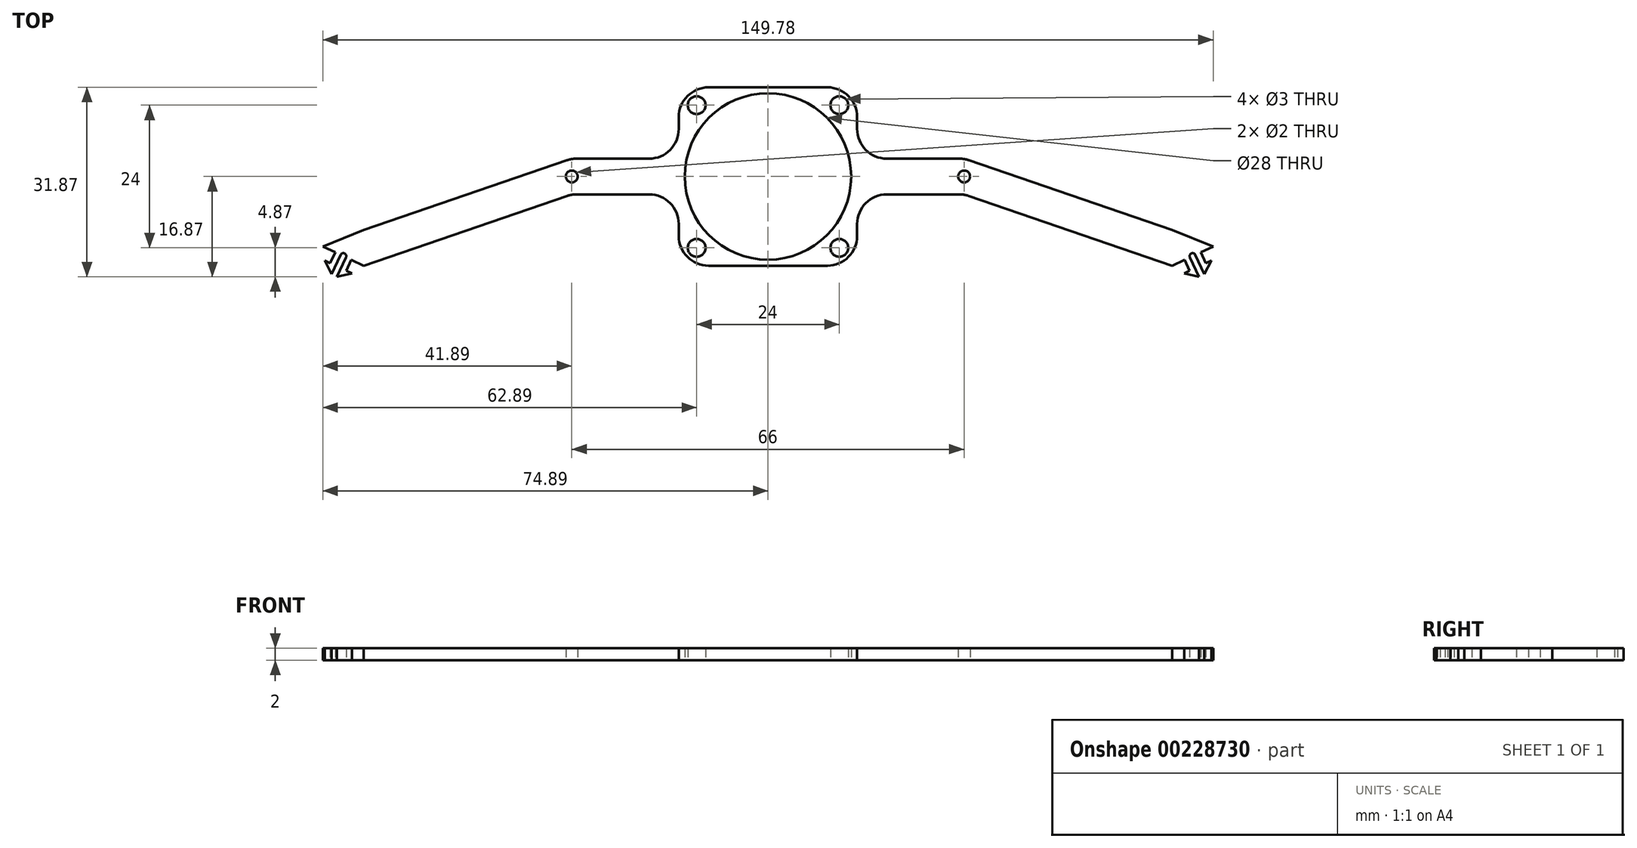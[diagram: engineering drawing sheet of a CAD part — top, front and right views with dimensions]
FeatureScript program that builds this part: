
annotation { "Feature Type Name" : "Feature", "Feature Type Description" : "" }
export const myFeature = defineFeature(function(context is Context, id is Id, definition is map)
    precondition{}
    {
        {
            var Q0;
            Q0=qCreatedBy(makeId("Top.planeOp"),FACE);
            var sketch = newSketch(context, id + "F0", { "sketchPlane" : qUnion([Q0])});
            skLineSegment(sketch, "E0.bottom", {"start": v(12, -12) * mm, "end": v(7.21, -12) * mm});
            skPoint(sketch, "E0.middle", {"position": v(0, 0) * mm});
            skCircle(sketch, "E1", {"center": v(-12, 12) * mm, "radius": 1.5 * mm});
            skCircle(sketch, "E2", {"center": v(12, 12) * mm, "radius": 1.5 * mm});
            skCircle(sketch, "E3", {"center": v(12, -12) * mm, "radius": 1.5 * mm});
            skCircle(sketch, "E4", {"center": v(-12, -12) * mm, "radius": 1.5 * mm});
            skCircle(sketch, "E5", {"center": v(0, 0) * mm, "radius": 14 * mm});
            skLineSegment(sketch, "E6.bottom", {"start": v(15, 15) * mm, "end": v(-15, 15) * mm});
            skLineSegment(sketch, "E6.top", {"start": v(15, -15) * mm, "end": v(-15, -15) * mm});
            skLineSegment(sketch, "E6.left", {"start": v(15, 15) * mm, "end": v(15, 3) * mm});
            skLineSegment(sketch, "E6.right", {"start": v(-15, 15) * mm, "end": v(-15, 3) * mm});
            skPoint(sketch, "E7.endSnap0", {"position": v(15, 0) * mm});
            skLineSegment(sketch, "E8.0", {"start": v(15, -3) * mm, "end": v(33, -3) * mm});
            skLineSegment(sketch, "E9.0", {"start": v(15, 3) * mm, "end": v(33, 3) * mm});
            skCircle(sketch, "E10", {"center": v(33, 0) * mm, "radius": 1 * mm});
            skLineSegment(sketch, "E11", {"start": v(68, -9) * mm, "end": v(33, 3) * mm});
            skLineSegment(sketch, "E12", {"start": v(33, -3) * mm, "end": v(68, -15) * mm});
            skLineSegment(sketch, "E13", {"start": v(68, -15) * mm, "end": v(70.09, -14.03) * mm});
            skLineSegment(sketch, "E14", {"start": v(68, -9) * mm, "end": v(74.9, -11.79) * mm});
            skLineSegment(sketch, "E15.0", {"start": v(72.8, -12.76) * mm, "end": v(73.65, -14.57) * mm});
            skLineSegment(sketch, "E16", {"start": v(73.65, -14.57) * mm, "end": v(74.58, -14.14) * mm});
            skLineSegment(sketch, "E17", {"start": v(74.58, -14.14) * mm, "end": v(73.42, -16.45) * mm});
            skLineSegment(sketch, "E18.MirrorCS", {"start": v(70, -16.27) * mm, "end": v(72.52, -16.87) * mm});
            skLineSegment(sketch, "E19.MirrorCS", {"start": v(70.93, -15.84) * mm, "end": v(70, -16.27) * mm});
            skLineSegment(sketch, "E20.MirrorCS", {"start": v(70.09, -14.03) * mm, "end": v(70.93, -15.84) * mm});
            skArc(sketch, "E21.0.startCap", {"start": v(71, -13.6) * mm, "mid": v(71.23, -12.94) * mm, "end": v(71.9, -13.18) * mm});
            skLineSegment(sketch, "E21.0.left", {"start": v(71.9, -13.18) * mm, "end": v(73.42, -16.45) * mm});
            skLineSegment(sketch, "E21.0.right", {"start": v(71, -13.6) * mm, "end": v(72.52, -16.87) * mm});
            skLineSegment(sketch, "E22.trimOffspring", {"start": v(72.8, -12.76) * mm, "end": v(74.9, -11.79) * mm});
            skPoint(sketch, "E23.orphan", {"position": v(73.14, -17.02) * mm});
            skLineSegment(sketch, "E24.trimOffspring", {"start": v(15, -3) * mm, "end": v(15, -15) * mm});
            skLineSegment(sketch, "E25.MirrorCS", {"start": v(-15, 3) * mm, "end": v(-33, 3) * mm});
            skLineSegment(sketch, "E26.MirrorCS", {"start": v(-15, -3) * mm, "end": v(-33, -3) * mm});
            skLineSegment(sketch, "E27.MirrorCS", {"start": v(-33, -3) * mm, "end": v(-68, -15) * mm});
            skLineSegment(sketch, "E28.MirrorCS", {"start": v(-68, -9) * mm, "end": v(-33, 3) * mm});
            skCircle(sketch, "E29.MirrorC", {"center": v(-33, 0) * mm, "radius": 1 * mm});
            skArc(sketch, "E30.MirrorCS", {"start": v(-71, -13.6) * mm, "mid": v(-71.23, -12.94) * mm, "end": v(-71.9, -13.18) * mm});
            skLineSegment(sketch, "E31.MirrorCS", {"start": v(-70, -16.27) * mm, "end": v(-72.52, -16.87) * mm});
            skLineSegment(sketch, "E32.MirrorCS", {"start": v(-70.09, -14.03) * mm, "end": v(-70.93, -15.84) * mm});
            skLineSegment(sketch, "E33.MirrorCS", {"start": v(-71, -13.6) * mm, "end": v(-72.52, -16.87) * mm});
            skLineSegment(sketch, "E34.MirrorCS", {"start": v(-73.65, -14.57) * mm, "end": v(-74.58, -14.14) * mm});
            skLineSegment(sketch, "E35.MirrorCS", {"start": v(-70.93, -15.84) * mm, "end": v(-70, -16.27) * mm});
            skLineSegment(sketch, "E36.MirrorCS", {"start": v(-72.8, -12.76) * mm, "end": v(-73.65, -14.57) * mm});
            skLineSegment(sketch, "E37.MirrorCS", {"start": v(-68, -15) * mm, "end": v(-70.09, -14.03) * mm});
            skLineSegment(sketch, "E38.MirrorCS", {"start": v(-72.8, -12.76) * mm, "end": v(-74.9, -11.79) * mm});
            skLineSegment(sketch, "E39.MirrorCS", {"start": v(-74.58, -14.14) * mm, "end": v(-73.42, -16.45) * mm});
            skLineSegment(sketch, "E40.MirrorCS", {"start": v(-71.9, -13.18) * mm, "end": v(-73.42, -16.45) * mm});
            skLineSegment(sketch, "E41.MirrorCS", {"start": v(-68, -9) * mm, "end": v(-74.9, -11.79) * mm});
            skPoint(sketch, "E42.MirrorP", {"position": v(-73.14, -17.02) * mm});
            skLineSegment(sketch, "E43.trimOffspring", {"start": v(-15, -3) * mm, "end": v(-15, -15) * mm});
            skSolve(sketch);
        }
        {
            var Q0;
            Q0 = qSketchRegion(id + "F0", true);
            extrude(context, id + "F1", {"entities" : qUnion([Q0]), "depth" : 2 * mm});
        }
        {
            var Q0;
            Q0=makeQuery(id+"F1.opExtrude","SWEPT_EDGE",EDGE,{"disambiguationData":[OSD([sQuery(id+"F0.wireOp",EDGE,"E8.0"),sQuery(id+"F0.wireOp",EDGE,"E12")])]});
            var Q1;
            Q1=makeQuery(id+"F1.opExtrude","SWEPT_EDGE",EDGE,{"disambiguationData":[OSD([sQuery(id+"F0.wireOp",EDGE,"E9.0"),sQuery(id+"F0.wireOp",EDGE,"E11")])]});
            var Q2;
            Q2=makeQuery(id+"F1.opExtrude","SWEPT_EDGE",EDGE,{"disambiguationData":[OSD([sQuery(id+"F0.wireOp",EDGE,"E6.left"),sQuery(id+"F0.wireOp",EDGE,"E9.0")])]});
            var Q3;
            Q3=makeQuery(id+"F1.opExtrude","SWEPT_EDGE",EDGE,{"disambiguationData":[OSD([sQuery(id+"F0.wireOp",EDGE,"E8.0"),sQuery(id+"F0.wireOp",EDGE,"E24.trimOffspring")])]});
            var Q4;
            Q4=makeQuery(id+"F1.opExtrude","SWEPT_EDGE",EDGE,{"disambiguationData":[OSD([sQuery(id+"F0.wireOp",EDGE,"E6.top"),sQuery(id+"F0.wireOp",EDGE,"E24.trimOffspring")])]});
            var Q5;
            Q5=makeQuery(id+"F1.opExtrude","SWEPT_EDGE",EDGE,{"disambiguationData":[OSD([sQuery(id+"F0.wireOp",EDGE,"E6.bottom"),sQuery(id+"F0.wireOp",EDGE,"E6.left")])]});
            var Q6;
            Q6=makeQuery(id+"F1.opExtrude","SWEPT_EDGE",EDGE,{"disambiguationData":[OSD([sQuery(id+"F0.wireOp",EDGE,"E6.bottom"),sQuery(id+"F0.wireOp",EDGE,"E6.right")])]});
            var Q7;
            Q7=makeQuery(id+"F1.opExtrude","SWEPT_EDGE",EDGE,{"disambiguationData":[OSD([sQuery(id+"F0.wireOp",EDGE,"E25.MirrorCS"),sQuery(id+"F0.wireOp",EDGE,"E28.MirrorCS")])]});
            var Q8;
            Q8=makeQuery(id+"F1.opExtrude","SWEPT_EDGE",EDGE,{"disambiguationData":[OSD([sQuery(id+"F0.wireOp",EDGE,"E6.top"),sQuery(id+"F0.wireOp",EDGE,"E43.trimOffspring")])]});
            var Q9;
            Q9=makeQuery(id+"F1.opExtrude","SWEPT_EDGE",EDGE,{"disambiguationData":[OSD([sQuery(id+"F0.wireOp",EDGE,"E26.MirrorCS"),sQuery(id+"F0.wireOp",EDGE,"E27.MirrorCS")])]});
            var Q10;
            Q10=makeQuery(id+"F1.opExtrude","SWEPT_EDGE",EDGE,{"disambiguationData":[OSD([sQuery(id+"F0.wireOp",EDGE,"E26.MirrorCS"),sQuery(id+"F0.wireOp",EDGE,"E43.trimOffspring")])]});
            var Q11;
            Q11=makeQuery(id+"F1.opExtrude","SWEPT_EDGE",EDGE,{"disambiguationData":[OSD([sQuery(id+"F0.wireOp",EDGE,"E6.right"),sQuery(id+"F0.wireOp",EDGE,"E25.MirrorCS")])]});
            fillet(context, id + "F2", {"entities" : qUnion([Q0, Q1, Q2, Q3, Q4, Q5, Q6, Q7, Q8, Q9, Q10, Q11]), "radius" : 5 * mm, "tangentPropagation" : true, "allowEdgeOverflow" : false});
        }
    });
